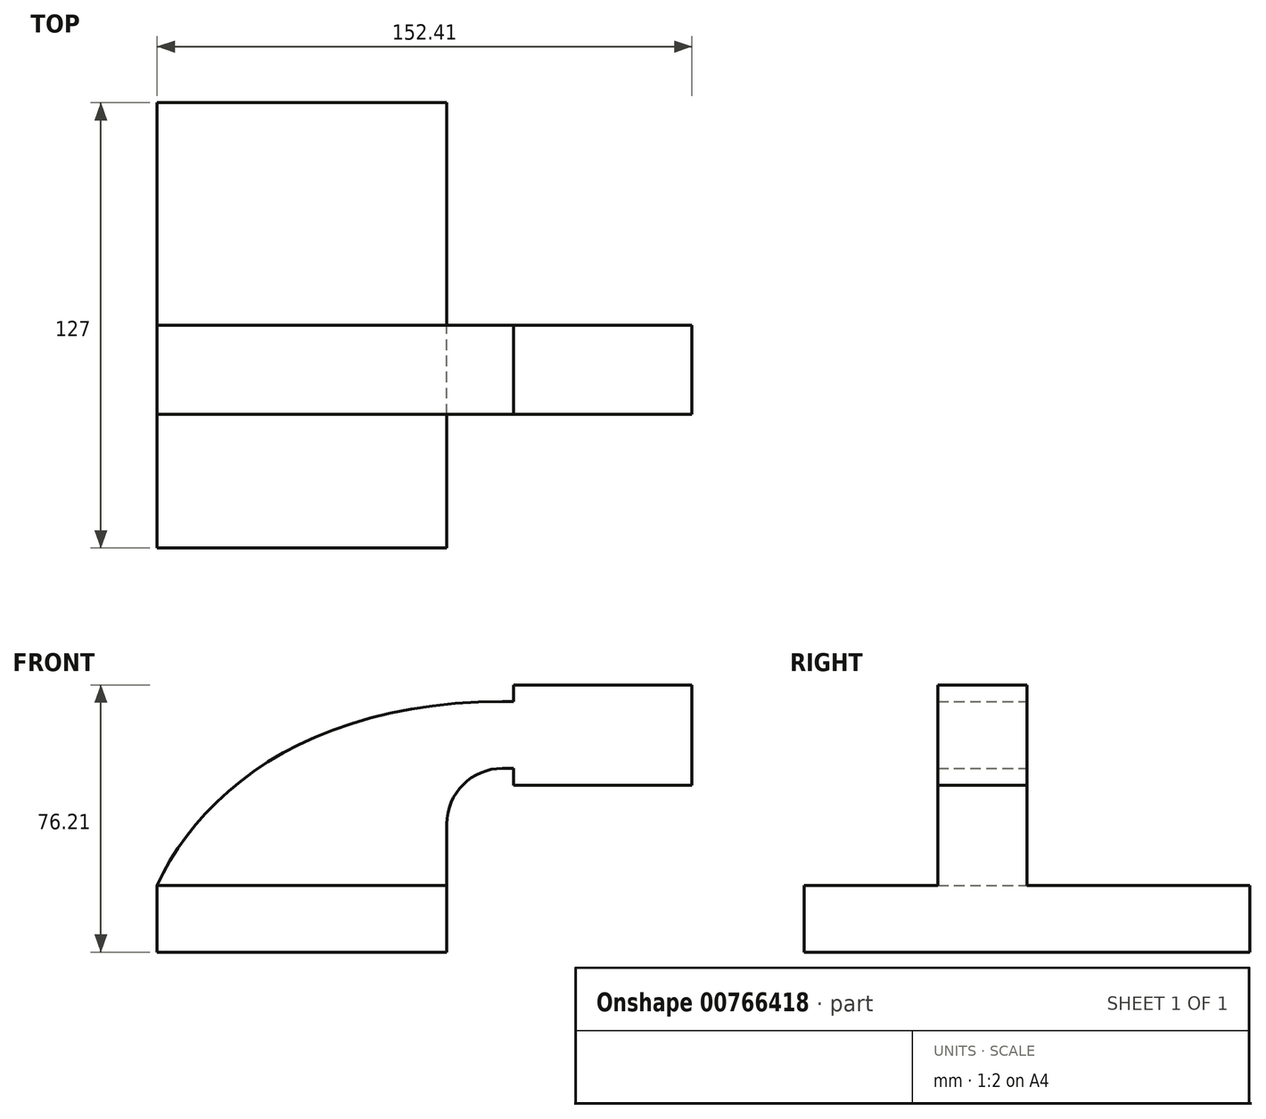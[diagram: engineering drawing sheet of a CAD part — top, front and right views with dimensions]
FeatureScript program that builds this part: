
annotation { "Feature Type Name" : "Feature", "Feature Type Description" : "" }
export const myFeature = defineFeature(function(context is Context, id is Id, definition is map)
    precondition{}
    {
        {
            var Q0;
            Q0=qCreatedBy(makeId("Front.planeOp"),FACE);
            var sketch = newSketch(context, id + "F0", { "sketchPlane" : qUnion([Q0])});
            skLineSegment(sketch, "E0.bottom", {"start": v(41.28, -9.53) * mm, "end": v(-41.28, -9.53) * mm});
            skLineSegment(sketch, "E0.top", {"start": v(41.28, 9.53) * mm, "end": v(-41.28, 9.53) * mm});
            skLineSegment(sketch, "E0.left", {"start": v(41.28, -9.52) * mm, "end": v(41.28, 9.53) * mm});
            skLineSegment(sketch, "E0.right", {"start": v(-41.28, -9.53) * mm, "end": v(-41.28, 9.53) * mm});
            skPoint(sketch, "E0.middle", {"position": v(0, 0) * mm});
            skLineSegment(sketch, "E1.bottom", {"start": v(111.12, 38.1) * mm, "end": v(60.32, 38.1) * mm});
            skLineSegment(sketch, "E1.top", {"start": v(111.12, 66.68) * mm, "end": v(60.32, 66.68) * mm});
            skLineSegment(sketch, "E1.left", {"start": v(111.12, 38.1) * mm, "end": v(111.12, 66.68) * mm});
            skLineSegment(sketch, "E1.right", {"start": v(60.32, 38.1) * mm, "end": v(60.32, 66.68) * mm});
            skPoint(sketch, "E1.middle", {"position": v(85.72, 52.39) * mm});
            skLineSegment(sketch, "E2", {"start": v(41.28, 9.53) * mm, "end": v(41.28, 27) * mm});
            skArc(sketch, "E3", {"start": v(41.27, 27) * mm, "mid": v(45.92, 38.23) * mm, "end": v(57.15, 42.88) * mm});
            skLineSegment(sketch, "E4", {"start": v(57.15, 42.88) * mm, "end": v(85.58, 42.88) * mm});
            skLineSegment(sketch, "E5.0", {"start": v(57.15, 61.93) * mm, "end": v(85.58, 61.93) * mm});
            skArc(sketch, "E5.1", {"start": v(22.23, 27) * mm, "mid": v(32.45, 51.7) * mm, "end": v(57.15, 61.93) * mm});
            skLineSegment(sketch, "E5.2", {"start": v(22.23, 9.6) * mm, "end": v(22.23, 27) * mm});
            skLineSegment(sketch, "E6", {"start": v(85.72, 38.1) * mm, "end": v(85.58, 66.68) * mm});
            skFitSpline(sketch, "E7", {"points": [v(-41.28, 9.53) * mm, v(57.15, 61.93) * mm], "startDerivative": vector(37.43, 82.32) * mm, "endDerivative": vector(161.28, 0) * mm});
            skSolve(sketch);
        }
        {
            var Q0;
            Q0=makeQuery(id+"F0.imprint","IMPRINT",FACE,{"disambiguationData":[TD([[makeQuery(id+"F0.imprint","IMPRINT",EDGE,{"derivedFrom":sQuery(id+"F0.wireOp",EDGE,"E0.bottom")}),-1.0]])]});
            extrude(context, id + "F1", {"entities" : qUnion([Q0]), "endBound" : BoundingType.SYMMETRIC, "depth" : 127 * mm, "offsetDistance" : 25.4 * mm});
        }
        {
            var Q0;
            Q0 = qSketchRegion(id + "F0", true);
            extrude(context, id + "F2", {"entities" : qUnion([Q0]), "operationType" : NewBodyOperationType.ADD, "depth" : 25.4 * mm, "offsetDistance" : 25.4 * mm});
        }
    });
